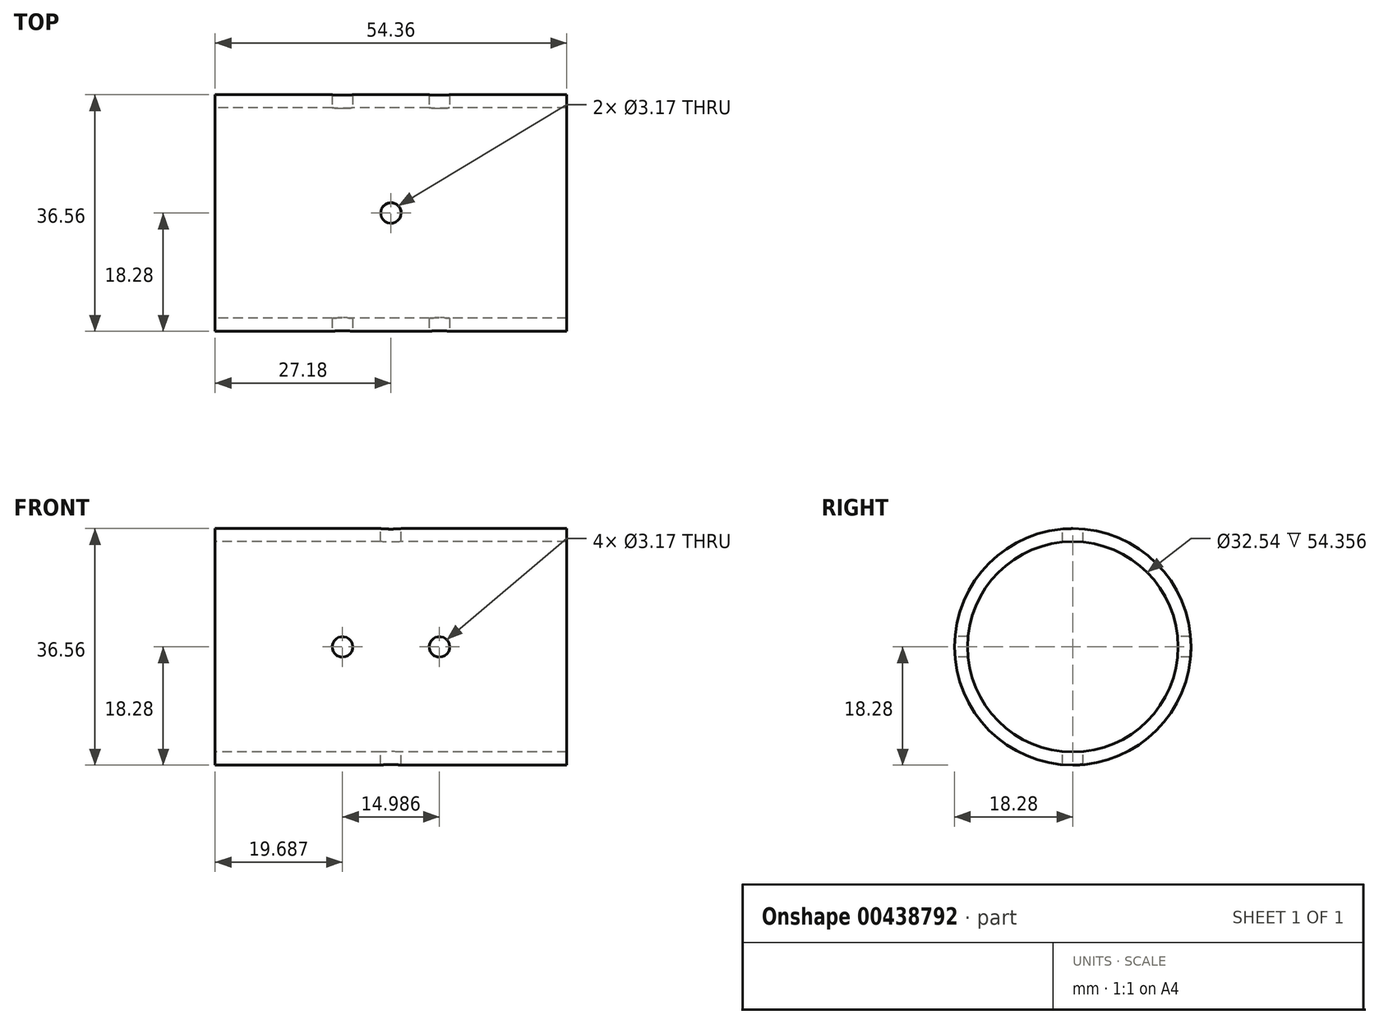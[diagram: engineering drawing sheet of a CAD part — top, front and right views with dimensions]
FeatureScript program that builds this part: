
annotation { "Feature Type Name" : "Feature", "Feature Type Description" : "" }
export const myFeature = defineFeature(function(context is Context, id is Id, definition is map)
    precondition{}
    {
        {
            var Q0;
            Q0=qCreatedBy(makeId("Right.planeOp"),FACE);
            var sketch = newSketch(context, id + "F0", { "sketchPlane" : qUnion([Q0])});
            skCircle(sketch, "E0", {"center": v(0, 0) * mm, "radius": 16.27 * mm});
            skCircle(sketch, "E1", {"center": v(0, 0) * mm, "radius": 18.28 * mm});
            skSolve(sketch);
        }
        {
            var Q0;
            Q0 = qSketchRegion(id + "F0", true);
            extrude(context, id + "F1", {"entities" : qUnion([Q0]), "depth" : 54.36 * mm, "symmetric" : true});
        }
        {
            var Q0;
            Q0=qCreatedBy(makeId("Top.planeOp"),FACE);
            var sketch = newSketch(context, id + "F2", { "sketchPlane" : qUnion([Q0])});
            skCircle(sketch, "E2", {"center": v(0, 0) * mm, "radius": 1.59 * mm});
            skSolve(sketch);
        }
        {
            var Q0;
            Q0 = qSketchRegion(id + "F2", true);
            extrude(context, id + "F3", {"entities" : qUnion([Q0]), "operationType" : NewBodyOperationType.REMOVE, "endBound" : BoundingType.THROUGH_ALL, "oppositeDirection" : true, "depth" : 25.4 * mm, "hasSecondDirection" : true, "secondDirectionBound" : BoundingType.THROUGH_ALL, "secondDirectionOppositeDirection" : false, "secondDirectionDepth" : 25.4 * mm});
        }
        {
            var Q0;
            Q0=qCreatedBy(makeId("Front.planeOp"),FACE);
            var sketch = newSketch(context, id + "F4", { "sketchPlane" : qUnion([Q0])});
            skCircle(sketch, "E3", {"center": v(-7.5, 0) * mm, "radius": 1.59 * mm});
            skCircle(sketch, "E4", {"center": v(7.5, 0) * mm, "radius": 1.59 * mm});
            skSolve(sketch);
        }
        {
            var Q0;
            Q0 = qSketchRegion(id + "F4", true);
            extrude(context, id + "F5", {"entities" : qUnion([Q0]), "operationType" : NewBodyOperationType.REMOVE, "endBound" : BoundingType.THROUGH_ALL, "oppositeDirection" : true, "depth" : 25.4 * mm, "hasSecondDirection" : true, "secondDirectionBound" : BoundingType.THROUGH_ALL, "secondDirectionOppositeDirection" : false, "secondDirectionDepth" : 25.4 * mm});
        }
    });
